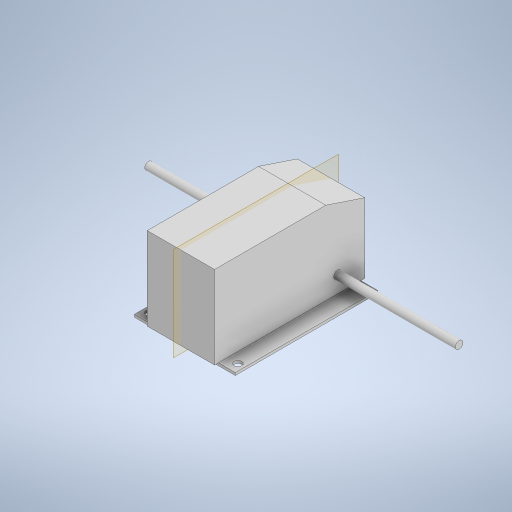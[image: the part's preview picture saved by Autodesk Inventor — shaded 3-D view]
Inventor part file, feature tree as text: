
AUTODESK INVENTOR PART (.ipt)
format: ipt  version: 2023.2 (Build 272271000, 271)  size: 315,904 bytes
history: native  units: mm
features: sketch x4
ambient origin geometry x8: Origin, YZ Plane, XZ Plane, XY Plane, X Axis, Y Axis, Z Axis, Center Point
bodies: Body1 (feature_tree)
feature tree (4):
  sketch  "Sketch1"  dims[d228=39.0mm]
  sketch  "Sketch2"  dims[d229=55.0mm]
  sketch  "Sketch3"  dims[d230=1.0mm d231=0.0mm]
  sketch  "Sketch4"  dims[d232=3.0mm d236=3.5mm d237=2.5mm d238=3.0mm d239=2.5mm d240=3.0mm d241=6.0mm d242=4.0mm d243=2.0mm d244=90.0deg d245=8.0mm d246=20.594885mm d249=32.0mm d250=0.0mm d251=15.0mm d252=5.0mm d253=45.0deg d257=26.0mm d258=58.0mm d259=6.5mm d260=1.5mm d272=3.0mm d273=10.5mm d274=6.5mm d275=120.0mm d276=0.0mm d9=0.5mm d10=0.872665mm d11=0.5mm d12=0.872665mm d13=0.5mm d14=0.872665mm d27=0.5mm d28=0.872665mm d29=0.5mm d30=0.872665mm d88=0.5mm d89=0.872665mm d90=0.5mm d91=0.872665mm d116=0.5mm d117=0.872665mm d118=0.5mm d119=0.872665mm d154=0.5mm d155=0.872665mm d156=0.5mm d157=0.872665mm d181=0.5mm d182=0.872665mm d183=0.5mm d184=0.872665mm d221=0.5mm d222=0.872665mm d223=0.5mm d224=0.872665mm d233=0.872665mm]
